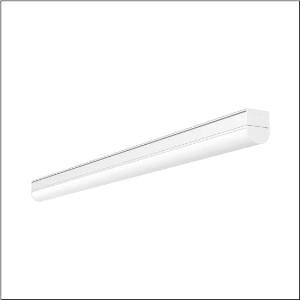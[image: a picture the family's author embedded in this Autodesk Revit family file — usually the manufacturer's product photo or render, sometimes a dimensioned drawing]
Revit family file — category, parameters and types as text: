
# Revit family: ecopack_31_51lj12dnm80a
name_source: partatom
category: Lighting Fixtures
units: mm (PartAtom-declared; Revit-internal decimal feet)

## family parameters
Cut with Voids When Loaded = No
Host = Face
Light Source = No
Part Type = Normal
Room Calculation Point = No
Round Connector Dimension = Use Diameter
Shared = No

## types (1)
- --- (1 x LED, 6780 lm, 52 W, 5000K)
    Apparent Load = 52 VA
    CIE Flux Codes = 39 67 87 89 100
    Color Rendering = 80
    Color Temperature = 5000K
    Default Elevation = 1800 mm
    Description = Ecopack 31, diffuser luminaire, primary optical cover: cover, of PC, frosted, light emission: direct distribution, primary light characteristic: symmetric, installation type: surface-mounted, LED, rated luminous flux: 7.000lm, luminous efficacy: 135lm/W, light colour: 830/840/850, colour temperature: 3000/4000/5000K, control gear: DALI 2, with terminal, 5-pole, mains connection: 220..240V, AC, 50/60Hz, rated input power: 52W, housing, of aluminium, traffic white (RAL 9016), length: 1.450mm, width: 56mm, height: 68mm, end cap, of PC, white, protection rating (complete): IP20, insulation class (complete): insulation class I (protective earthing), certification: CE, impact resistance: IK06, permissible operating ambient temperature: -20..+40°C, packaging unit: 1 piece
    Height = 68 mm
    Lamp = 1 x LED
    Lamp Light Flux = 6780 lm
    Lamp Power = 52 W
    Lamp count = 1
    Length = 1450 mm
    Luminous efficacy = 130 lm/W
    Manufacturer = Siteco
    ModVariant = No
    Model = 51LJ12DNM80A
    Mounting Place = Ceiling
    Mounting Type = Surface mounted
    Number of Poles = 1
    OnlyDefault = Yes
    Power Factor = 1
    Product Name = Ecopack 31
    Product group = diffuser luminaire
    ProductGroupID = 307
    Protection Class = Protection class I
    Protection Degree = IP 20
    RLX_Detail_Level = 1
    RLX_Emergency_Light_Flux = 0 lm
    RLX_Emergency_Type = 0
    RLX_Emergency_Type_DB = No
    RlxData = <blob elided: 21629 chars, md5=14eec168>
    Socket = socket
    Standby Power = 0 W
    System Light Flux = 6780 lm
    System Power = 52 W
    Type Comments = individual setting: colour temperature 5000K
    Type Image = l_1007033.jpg
    URL = http://relux.com
    VarID = @adj_174985
    Voltage = 0 V
    Weight = 0.00 kg
    Width = 56 mm

## geometry (parser evidence)
native form markers: Blend x4, Sweep x15
no freeform markers — native parametric forms only
